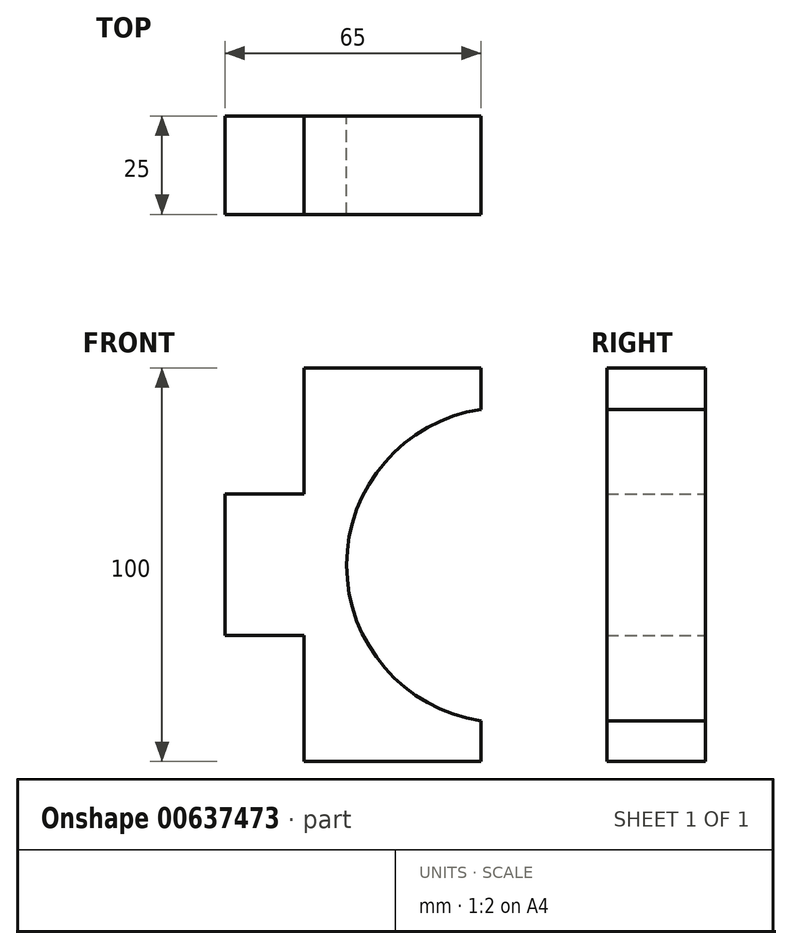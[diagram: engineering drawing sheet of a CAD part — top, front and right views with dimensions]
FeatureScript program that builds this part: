
annotation { "Feature Type Name" : "Feature", "Feature Type Description" : "" }
export const myFeature = defineFeature(function(context is Context, id is Id, definition is map)
    precondition{}
    {
        {
            var Q0;
            Q0=qCreatedBy(makeId("Front.planeOp"),FACE);
            var sketch = newSketch(context, id + "F0", { "sketchPlane" : qUnion([Q0])});
            skLineSegment(sketch, "E0.bottom", {"start": v(-34.32, 43.92) * mm, "end": v(10.68, 43.92) * mm});
            skLineSegment(sketch, "E0.top", {"start": v(-34.32, -56.08) * mm, "end": v(10.68, -56.08) * mm});
            skLineSegment(sketch, "E0.left", {"start": v(-34.32, 43.92) * mm, "end": v(-34.32, -56.08) * mm});
            skLineSegment(sketch, "E0.right", {"start": v(10.68, 43.92) * mm, "end": v(10.68, 33.38) * mm});
            skLineSegment(sketch, "E1.bottom", {"start": v(-34.32, 11.92) * mm, "end": v(-54.32, 11.92) * mm});
            skLineSegment(sketch, "E1.top", {"start": v(-34.32, -24.08) * mm, "end": v(-54.32, -24.08) * mm});
            skLineSegment(sketch, "E1.right", {"start": v(-54.32, 11.92) * mm, "end": v(-54.32, -24.08) * mm});
            skArc(sketch, "E2", {"start": v(10.68, 33.38) * mm, "mid": v(-23.44, -6.18) * mm, "end": v(10.68, -45.75) * mm});
            skPoint(sketch, "E3.orphan", {"position": v(10.68, -6.08) * mm});
            skPoint(sketch, "E4.end.orphan", {"position": v(-54.32, -6.08) * mm});
            skPoint(sketch, "E5.start.orphan", {"position": v(-34.32, -6.08) * mm});
            skLineSegment(sketch, "E6.trimOffspring", {"start": v(10.68, -45.75) * mm, "end": v(10.68, -56.08) * mm});
            skSolve(sketch);
        }
        {
            var Q0;
            Q0 = qSketchRegion(id + "F0", true);
            extrude(context, id + "F1", {"entities" : qUnion([Q0]), "depth" : 25 * mm, "offsetDistance" : 25 * mm});
        }
    });
